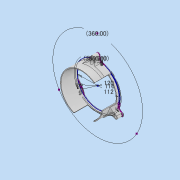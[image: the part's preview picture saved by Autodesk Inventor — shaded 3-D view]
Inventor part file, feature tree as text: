
AUTODESK INVENTOR PART (.ipt)
format: ipt  version: 2022 (Build 260153000, 153)  size: 493,056 bytes
history: native  units: mm
features: fillet x11, extrude x8, other x2, pattern_circular x1
ambient origin geometry x8: Origin, YZ Plane, XZ Plane, XY Plane, X Axis, Y Axis, Z Axis, Center Point
bodies: Body1 (feature_tree)
feature tree (22):
  other  "ソリッド1"
  other  "baseSC"
  extrude  "押し出し4"  Depth=120.0mm
  extrude  "押し出し5"  Depth=112.0mm
  extrude  "押し出し6"  Depth=9.0mm
  extrude  "押し出し7"  Depth=6.0mm
  extrude  "押し出し8"  Depth=6.0mm
  fillet  "フィレット3"  Radius=9.0mm
  pattern_circular  "円形状パターン4"  Count=3 Angle=360.0deg
  fillet  "フィレット4"  Radius=9.0mm
  fillet  "フィレット5"  Radius=9.0mm
  fillet  "フィレット6"  Radius=9.0mm
  extrude  "押し出し9"  Depth=30.0mm TaperAngle=360.0deg
  extrude  "押し出し10"  Depth=116.0mm
  extrude  "押し出し11"  Depth=2.0mm TaperAngle=0.0deg
  fillet  "フィレット7"  Radius=30.0mm
  fillet  "フィレット8"  Radius=1.5mm
  fillet  "フィレット9"  Radius=14.0mm
  fillet  "フィレット10"  Radius=44.0mm
  fillet  "フィレット11"  Radius=44.0mm
  fillet  "フィレット12"  Radius=6.0mm
  fillet  "フィレット13"  Radius=1.9mm
